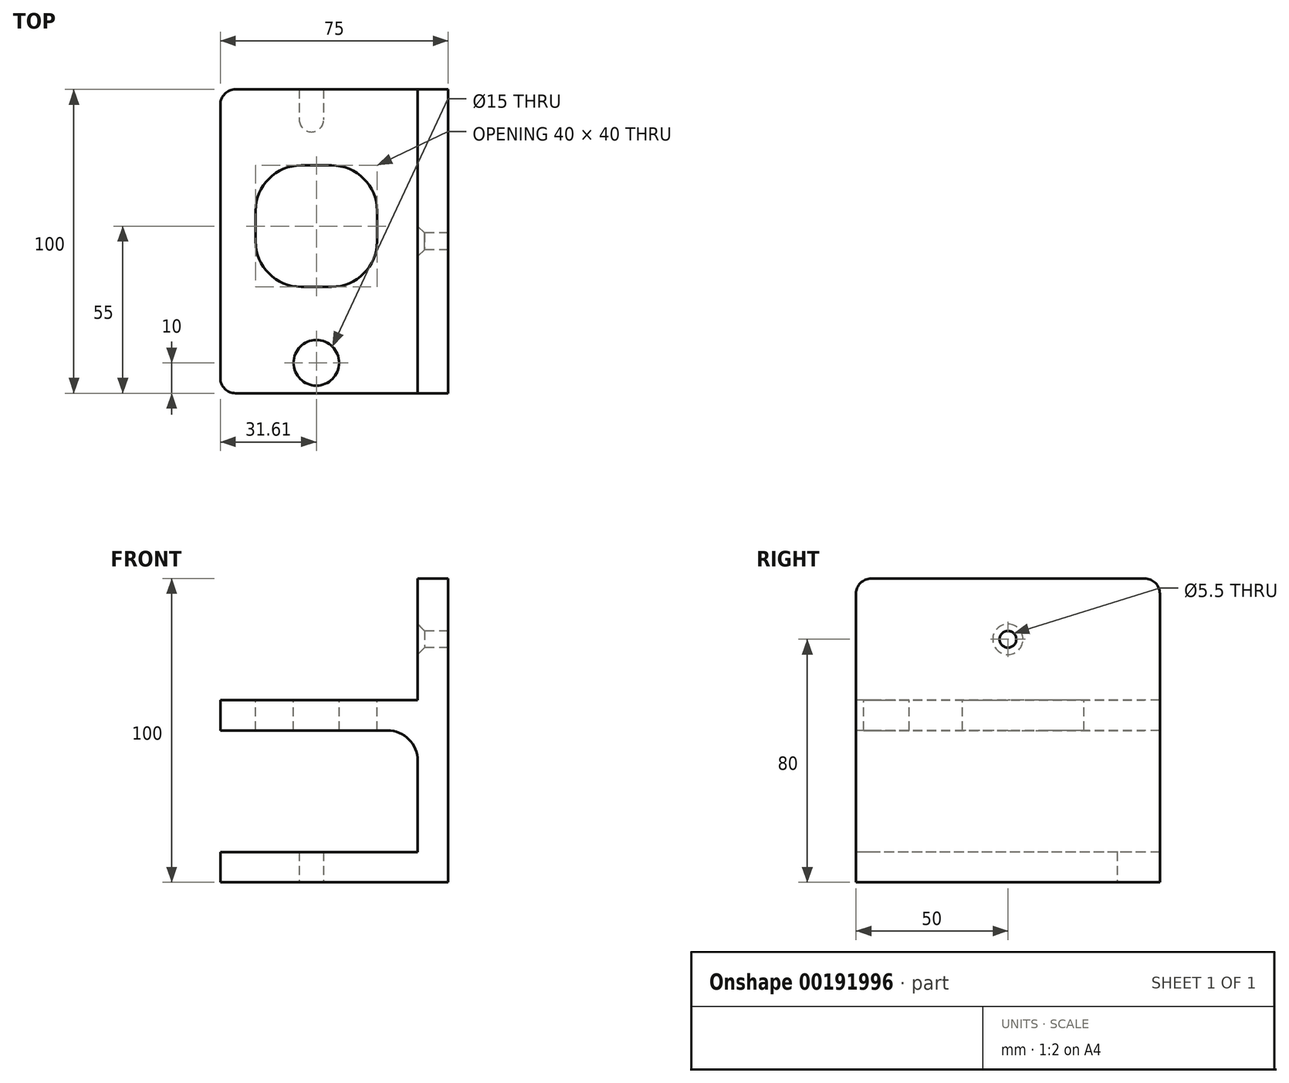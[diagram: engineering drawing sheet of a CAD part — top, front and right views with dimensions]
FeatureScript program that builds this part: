
annotation { "Feature Type Name" : "Feature", "Feature Type Description" : "" }
export const myFeature = defineFeature(function(context is Context, id is Id, definition is map)
    precondition{}
    {
        {
            var Q0;
            Q0=qCreatedBy(makeId("Top.planeOp"),FACE);
            var sketch = newSketch(context, id + "F0", { "sketchPlane" : qUnion([Q0])});
            skLineSegment(sketch, "E0.bottom", {"start": v(-37.5, 50) * mm, "end": v(-11.5, 50) * mm});
            skLineSegment(sketch, "E0.top", {"start": v(-37.5, -50) * mm, "end": v(37.5, -50) * mm});
            skLineSegment(sketch, "E0.left", {"start": v(-37.5, 50) * mm, "end": v(-37.5, -50) * mm});
            skLineSegment(sketch, "E0.right", {"start": v(37.5, 50) * mm, "end": v(37.5, -50) * mm});
            skPoint(sketch, "E0.middle", {"position": v(0, 0) * mm});
            skLineSegment(sketch, "E1.left", {"start": v(-11.5, 50) * mm, "end": v(-11.5, 40) * mm});
            skLineSegment(sketch, "E1.right", {"start": v(-3.5, 50) * mm, "end": v(-3.5, 40) * mm});
            skArc(sketch, "E2", {"start": v(-11.5, 40) * mm, "mid": v(-7.5, 36) * mm, "end": v(-3.5, 40) * mm});
            skLineSegment(sketch, "E3.trimOffspring", {"start": v(-3.5, 50) * mm, "end": v(37.5, 50) * mm});
            skSolve(sketch);
        }
        {
            var Q0;
            Q0=makeQuery(id+"F0.imprint","IMPRINT",FACE,{"disambiguationData":[TD([[makeQuery(id+"F0.imprint","IMPRINT",EDGE,{"derivedFrom":sQuery(id+"F0.wireOp",EDGE,"E0.bottom")}),-1.0]])]});
            extrude(context, id + "F1", {"entities" : qUnion([Q0]), "depth" : 10 * mm});
        }
        {
            var Q0;
            Q0=makeQuery(id+"F1.opExtrude","SWEPT_FACE",FACE,{"disambiguationData":[OSD([sQuery(id+"F0.wireOp",EDGE,"E0.right")])]});
            var sketch = newSketch(context, id + "F2", { "sketchPlane" : qUnion([Q0])});
            skLineSegment(sketch, "E4.bottom", {"start": v(-50, 0) * mm, "end": v(50, 0) * mm});
            skLineSegment(sketch, "E4.top", {"start": v(-50, 100) * mm, "end": v(50, 100) * mm});
            skLineSegment(sketch, "E4.left", {"start": v(-50, 0) * mm, "end": v(-50, 100) * mm});
            skLineSegment(sketch, "E4.right", {"start": v(50, 0) * mm, "end": v(50, 100) * mm});
            skSolve(sketch);
        }
        {
            var Q0;
            {var subQ0=sQuery(id+"F2.wireOp",EDGE,"E4.top");Q0=makeQuery(id+"F2.imprint","IMPRINT",FACE,{"disambiguationData":[TD([[makeQuery(id+"F2.imprint","IMPRINT",EDGE,{"derivedFrom":subQ0}),-1.0]])]});}
            extrude(context, id + "F3", {"entities" : qUnion([Q0]), "operationType" : NewBodyOperationType.ADD, "oppositeDirection" : true, "depth" : 10 * mm});
        }
        {
            var Q0;
            Q0=makeQuery(id+"F3.opExtrude","CAP_FACE",FACE,{"disambiguationData":[OSD([sQuery(id+"F0.wireOp",EDGE,"E0.right"),sQuery(id+"F2.wireOp",EDGE,"E4.top"),sQuery(id+"F2.wireOp",EDGE,"E4.left"),sQuery(id+"F2.wireOp",EDGE,"E4.right")])],"isStart":false});
            var sketch = newSketch(context, id + "F4", { "sketchPlane" : qUnion([Q0])});
            skPoint(sketch, "E5", {"position": v(0, 80) * mm});
            skSolve(sketch);
        }
        {
            var Q0;
            Q0=makeQuery(id+"F3.opExtrude","CAP_FACE",FACE,{"disambiguationData":[OSD([sQuery(id+"F0.wireOp",EDGE,"E0.right"),sQuery(id+"F2.wireOp",EDGE,"E4.top"),sQuery(id+"F2.wireOp",EDGE,"E4.left"),sQuery(id+"F2.wireOp",EDGE,"E4.right")])],"isStart":false});
            var sketch = newSketch(context, id + "F5", { "sketchPlane" : qUnion([Q0])});
            skLineSegment(sketch, "E6.bottom", {"start": v(-50, 60) * mm, "end": v(50, 60) * mm});
            skLineSegment(sketch, "E6.top", {"start": v(-50, 50) * mm, "end": v(50, 50) * mm});
            skLineSegment(sketch, "E6.left", {"start": v(-50, 60) * mm, "end": v(-50, 50) * mm});
            skLineSegment(sketch, "E6.right", {"start": v(50, 60) * mm, "end": v(50, 50) * mm});
            skSolve(sketch);
        }
        {
            var Q0;
            Q0 = qSketchRegion(id + "F5", true);
            var Q1;
            Q1=makeQuery(id+"F1.opExtrude","SWEPT_FACE",FACE,{"disambiguationData":[OSD([sQuery(id+"F0.wireOp",EDGE,"E0.left")])]});
            extrude(context, id + "F6", {"entities" : qUnion([Q0]), "operationType" : NewBodyOperationType.ADD, "endBound" : BoundingType.UP_TO_SURFACE, "endBoundEntityFace" : qUnion([Q1]), "depth" : 25 * mm});
        }
        {
            var Q0;
            Q0=sQuery(id+"F4.wireOp",VERTEX,"E5");
            var Q1;
            Q1=makeQuery(id+"F1.opExtrude","SWEPT_BODY",BODY,{"disambiguationData":[OSD([sQuery(id+"F0.wireOp",EDGE,"E0.bottom"),sQuery(id+"F0.wireOp",EDGE,"E0.top"),sQuery(id+"F0.wireOp",EDGE,"E0.left"),sQuery(id+"F0.wireOp",EDGE,"E0.right")])]});
            hole(context, id + "F7", {"style" : HoleStyle.C_SINK, "endStyle" : HoleEndStyle.THROUGH, "holeDiameter" : 5.5 * mm, "cSinkDiameter" : 10 * mm, "cSinkAngle" : 90 * degree, "locations" : qUnion([Q0]), "scope" : qUnion([Q1]), "isTappedThrough" : true});
        }
        {
            var Q0;
            Q0=makeQuery(id+"F1.opExtrude","SWEPT_EDGE",EDGE,{"disambiguationData":[OSD([sQuery(id+"F0.wireOp",EDGE,"E0.bottom"),sQuery(id+"F0.wireOp",EDGE,"E0.left")])]});
            var Q1;
            Q1=makeQuery(id+"F1.opExtrude","SWEPT_EDGE",EDGE,{"disambiguationData":[OSD([sQuery(id+"F0.wireOp",EDGE,"E0.top"),sQuery(id+"F0.wireOp",EDGE,"E0.left")])]});
            var Q2;
            Q2=makeQuery(id+"F3.opExtrude","SWEPT_EDGE",EDGE,{"disambiguationData":[OSD([sQuery(id+"F2.wireOp",EDGE,"E4.top"),sQuery(id+"F2.wireOp",EDGE,"E4.left")])]});
            var Q3;
            Q3=makeQuery(id+"F3.opExtrude","SWEPT_EDGE",EDGE,{"disambiguationData":[OSD([sQuery(id+"F2.wireOp",EDGE,"E4.top"),sQuery(id+"F2.wireOp",EDGE,"E4.right")])]});
            var Q4;
            Q4=makeQuery(id+"F6.opExtrude","CAP_EDGE",EDGE,{"disambiguationData":[OSD([sQuery(id+"F5.wireOp",EDGE,"E6.left")])],"isStart":false});
            var Q5;
            Q5=makeQuery(id+"F6.opExtrude","CAP_EDGE",EDGE,{"disambiguationData":[OSD([sQuery(id+"F5.wireOp",EDGE,"E6.right")])],"isStart":false});
            fillet(context, id + "F8", {"entities" : qUnion([Q0, Q1, Q2, Q3, Q4, Q5]), "radius" : 5 * mm, "tangentPropagation" : true, "allowEdgeOverflow" : false});
        }
        {
            var Q0;
            Q0=makeQuery(id+"F3.opExtrude","CAP_EDGE",EDGE,{"disambiguationData":[OSD([sQuery(id+"F0.wireOp",EDGE,"E0.right")])],"isStart":false});
            var Q1;
            Q1=makeQuery(id+"F6.opExtrude","CAP_EDGE",EDGE,{"disambiguationData":[OSD([sQuery(id+"F5.wireOp",EDGE,"E6.bottom")])],"isStart":true});
            var Q2;
            Q2=makeQuery(id+"F6.opExtrude","CAP_EDGE",EDGE,{"disambiguationData":[OSD([sQuery(id+"F5.wireOp",EDGE,"E6.top")])],"isStart":true});
            fillet(context, id + "F9", {"entities" : qUnion([Q0, Q1, Q2]), "radius" : 10 * mm, "tangentPropagation" : true, "allowEdgeOverflow" : false});
        }
        {
            var Q0;
            Q0=makeQuery(id+"F6.opExtrude","SWEPT_FACE",FACE,{"disambiguationData":[OSD([sQuery(id+"F5.wireOp",EDGE,"E6.bottom")])]});
            var sketch = newSketch(context, id + "F10", { "sketchPlane" : qUnion([Q0])});
            skCircle(sketch, "E7", {"center": v(-5.89, -40) * mm, "radius": 7.5 * mm});
            skLineSegment(sketch, "E8.bottom", {"start": v(-10.89, 25) * mm, "end": v(-0.89, 25) * mm});
            skLineSegment(sketch, "E8.top", {"start": v(-10.89, -15) * mm, "end": v(-0.89, -15) * mm});
            skLineSegment(sketch, "E8.left", {"start": v(-25.89, 10) * mm, "end": v(-25.89, 0) * mm});
            skLineSegment(sketch, "E8.right", {"start": v(14.11, 10) * mm, "end": v(14.11, 0) * mm});
            skPoint(sketch, "E9.visualSharp", {"position": v(-25.89, 25) * mm});
            skArc(sketch, "E9.filletArc", {"start": v(-10.89, 25) * mm, "mid": v(-21.5, 20.6) * mm, "end": v(-25.89, 10) * mm});
            skPoint(sketch, "E10.visualSharp", {"position": v(14.11, 25) * mm});
            skArc(sketch, "E10.filletArc", {"start": v(14.11, 10) * mm, "mid": v(9.72, 20.6) * mm, "end": v(-0.89, 25) * mm});
            skPoint(sketch, "E11.visualSharp", {"position": v(-25.89, -15) * mm});
            skArc(sketch, "E11.filletArc", {"start": v(-25.89, 0) * mm, "mid": v(-21.5, -10.6) * mm, "end": v(-10.89, -15) * mm});
            skPoint(sketch, "E12.visualSharp", {"position": v(14.11, -15) * mm});
            skArc(sketch, "E12.filletArc", {"start": v(-0.89, -15) * mm, "mid": v(9.72, -10.6) * mm, "end": v(14.11, 0) * mm});
            skLineSegment(sketch, "E13", {"start": v(-5.89, -15) * mm, "end": v(-5.89, -40) * mm, "construction": true});
            skSolve(sketch);
        }
        {
            var Q0;
            Q0 = qSketchRegion(id + "F10", true);
            extrude(context, id + "F11", {"entities" : qUnion([Q0]), "operationType" : NewBodyOperationType.REMOVE, "endBound" : BoundingType.UP_TO_NEXT, "oppositeDirection" : true, "depth" : 25 * mm});
        }
    });
